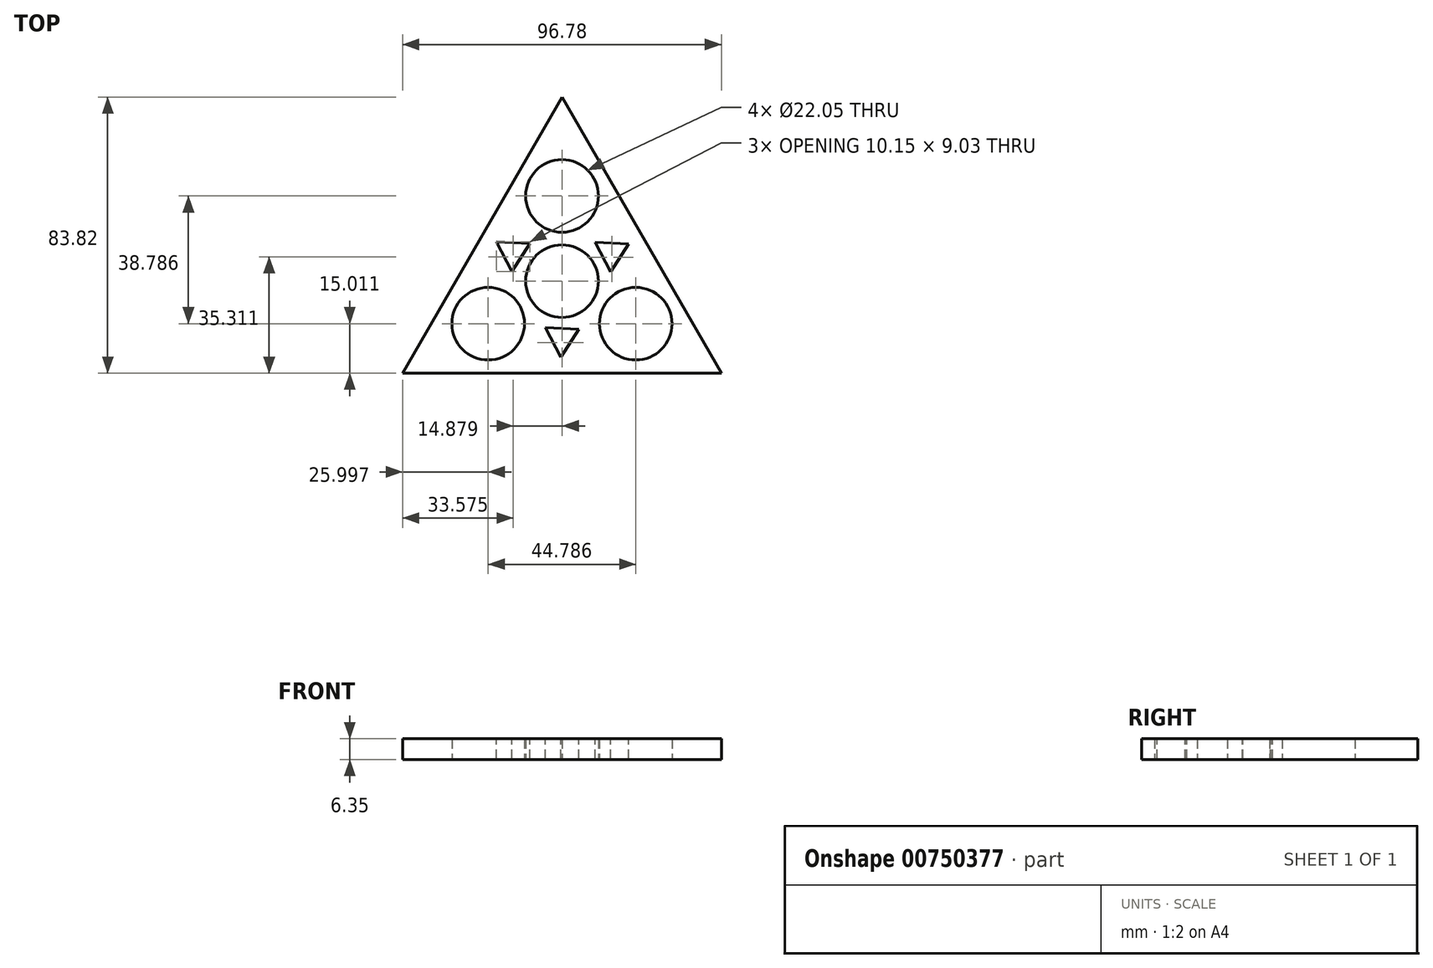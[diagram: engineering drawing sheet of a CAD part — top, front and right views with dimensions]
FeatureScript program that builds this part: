
annotation { "Feature Type Name" : "Feature", "Feature Type Description" : "" }
export const myFeature = defineFeature(function(context is Context, id is Id, definition is map)
    precondition{}
    {
        {
            var Q0;
            Q0=qCreatedBy(makeId("Top.planeOp"),FACE);
            var sketch = newSketch(context, id + "F0", { "sketchPlane" : qUnion([Q0])});
            skCircle(sketch, "E0", {"center": v(0, 0) * mm, "radius": 11.02 * mm});
            skCircle(sketch, "E1.cCircle", {"center": v(0, 0) * mm, "radius": 27.94 * mm, "construction": true});
            skLineSegment(sketch, "E1.0", {"start": v(48.4, -27.94) * mm, "end": v(-48.4, -27.94) * mm});
            skLineSegment(sketch, "E1.1", {"start": v(-48.4, -27.94) * mm, "end": v(0, 55.88) * mm});
            skLineSegment(sketch, "E1.2", {"start": v(0, 55.88) * mm, "end": v(48.4, -27.94) * mm});
            skPoint(sketch, "E1.0.midPoint", {"position": v(0, -27.94) * mm});
            skCircle(sketch, "E2", {"center": v(-22.4, -12.93) * mm, "radius": 11.02 * mm});
            skCircle(sketch, "E3.1.0", {"center": v(22.4, -12.93) * mm, "radius": 11.02 * mm});
            skCircle(sketch, "E3.2.0", {"center": v(0, 25.86) * mm, "radius": 11.02 * mm});
            skSolve(sketch);
        }
        {
            var Q0;
            Q0=makeQuery(id+"F0.imprint","IMPRINT",FACE,{"disambiguationData":[TD([[makeQuery(id+"F0.imprint","IMPRINT",EDGE,{"derivedFrom":sQuery(id+"F0.wireOp",EDGE,"E0")}),-1.0]])]});
            extrude(context, id + "F1", {"entities" : qUnion([Q0]), "depth" : 6.35 * mm, "offsetDistance" : 25.4 * mm});
        }
        {
            var Q0;
            Q0=makeQuery(id+"F1.opExtrude","CAP_FACE",FACE,{"disambiguationData":[OSD([sQuery(id+"F0.wireOp",EDGE,"E0"),sQuery(id+"F0.wireOp",EDGE,"E1.0"),sQuery(id+"F0.wireOp",EDGE,"E1.1"),sQuery(id+"F0.wireOp",EDGE,"E1.2"),sQuery(id+"F0.wireOp",EDGE,"E2"),sQuery(id+"F0.wireOp",EDGE,"E3.1.0"),sQuery(id+"F0.wireOp",EDGE,"E3.2.0")])],"isStart":false});
            var sketch = newSketch(context, id + "F2", { "sketchPlane" : qUnion([Q0])});
            skLineSegment(sketch, "E4", {"start": v(-19.89, 11.88) * mm, "end": v(-15.23, 2.86) * mm});
            skLineSegment(sketch, "E5", {"start": v(-15.23, 2.86) * mm, "end": v(-9.74, 11.4) * mm});
            skLineSegment(sketch, "E6", {"start": v(-9.74, 11.4) * mm, "end": v(-19.89, 11.88) * mm});
            skLineSegment(sketch, "E7.1.0", {"start": v(-5.01, -14.14) * mm, "end": v(-0.35, -23.17) * mm});
            skLineSegment(sketch, "E7.1.1", {"start": v(-0.35, -23.17) * mm, "end": v(5.14, -14.61) * mm});
            skLineSegment(sketch, "E7.1.2", {"start": v(5.14, -14.61) * mm, "end": v(-5.01, -14.14) * mm});
            skLineSegment(sketch, "E7.2.0", {"start": v(14.75, 2.73) * mm, "end": v(20.24, 11.28) * mm});
            skLineSegment(sketch, "E7.2.1", {"start": v(20.24, 11.28) * mm, "end": v(10.09, 11.76) * mm});
            skLineSegment(sketch, "E7.2.2", {"start": v(10.09, 11.76) * mm, "end": v(14.75, 2.73) * mm});
            skPoint(sketch, "E7.center", {"position": v(0, 0) * mm});
            skSolve(sketch);
        }
        {
            var Q0;
            Q0=makeQuery(id+"F2.imprint","IMPRINT",FACE,{"disambiguationData":[TD([[makeQuery(id+"F2.imprint","IMPRINT",EDGE,{"derivedFrom":sQuery(id+"F2.wireOp",EDGE,"E4")}),1.0]])]});
            var Q1;
            Q1=makeQuery(id+"F2.imprint","IMPRINT",FACE,{"disambiguationData":[TD([[makeQuery(id+"F2.imprint","IMPRINT",EDGE,{"derivedFrom":sQuery(id+"F2.wireOp",EDGE,"E7.1.0")}),1.0]])]});
            var Q2;
            Q2=makeQuery(id+"F2.imprint","IMPRINT",FACE,{"disambiguationData":[TD([[makeQuery(id+"F2.imprint","IMPRINT",EDGE,{"derivedFrom":sQuery(id+"F2.wireOp",EDGE,"E7.2.0")}),1.0]])]});
            extrude(context, id + "F3", {"entities" : qUnion([Q0, Q1, Q2]), "operationType" : NewBodyOperationType.REMOVE, "oppositeDirection" : true, "depth" : 6.35 * mm, "offsetDistance" : 25.4 * mm});
        }
    });
